# Revit family: Casement_30.5_D_Top_Hung_Standard
name_source: partatom
category: Windows
revit_build: Autodesk Revit 2014 (Build: 20130308_1515(x64)
units: mm (PartAtom-declared; Revit-internal decimal feet)

## types (12) — shared parameters
Aluminium Thickness = 1 mm  [stored 0.00328084 ft]
Bead SG Gap = 13 mm  [stored 0.0426509 ft]
Bottom Hung = No
Casement Dimension = 31 mm  [stored 0.101706 ft]
Custom Sash Height = 554 mm  [stored 1.81759 ft]
DG Extrusion Start = 5 mm  [stored 0.0164042 ft]
DG Gasket Finish = Double Glazing Gasket Material
DG Thickness = 3 mm  [stored 0.00984252 ft]
DG Thickness Calc = 3 mm  [stored 0.00984252 ft]
Default Sill Height = 800 mm  [stored 2.62467 ft]
Depth Bead = 17 mm
Description = Window 30.5mm, Type D top hung
Double Glazing = No
Frame Center Offset = 15 mm  [stored 0.0492126 ft]
Height Panel 1 = 540 mm  [stored 1.77165 ft]
Height Sash = 524 mm  [stored 1.71916 ft]
Height Sash Opening = 554 mm  [stored 1.81759 ft]
Limit Fixed Pane Height Max = 1800 mm  [stored 5.90551 ft]
Limit Fixed Pane Height Min = 200 mm  [stored 0.656168 ft]
Limit Sash Height Max = 750 mm  [stored 2.46063 ft]
Limit Sash Height Min = 300 mm  [stored 0.984252 ft]
Limit Sash Width Max = 1000 mm  [stored 3.28084 ft]
Limit Sash Width Min = 300 mm  [stored 0.984252 ft]
Limit Window Height Max = 2430 mm
Limit Window Height Min = 830 mm  [stored 2.7231 ft]
Limit Window Width Max = 1046 mm  [stored 3.43176 ft]
Limit Window Width Min = 346 mm
Manufacturer = Crealco
Max System DG One Piece Thickness = 3 mm  [stored 0.00984252 ft]
Max System DG Unit Thickness = 18 mm  [stored 0.0590551 ft]
Model = Casement 30.5
Offset Bead SG Center Reversed = 15 mm  [stored 0.0492126 ft]
Offset Panel 3 Bead Top = 600 mm  [stored 1.9685 ft]
Offset Sash Left = 23 mm  [stored 0.0754593 ft]
Offset Sash Top = 23 mm  [stored 0.0754593 ft]
Offset Transom Top = 570 mm  [stored 1.87008 ft]
Offset Window Exterior = 15 mm  [stored 0.0492126 ft]
SG Gasket Thickness = 6 mm  [stored 0.019685 ft]
Sash Center Offset = 12 mm  [stored 0.0393701 ft]
Sash Overlap = 7 mm  [stored 0.0229659 ft]
Sash Spacing Inner = 8 mm  [stored 0.0262467 ft]
Top Hung = Yes
URL = http://www.crealco.co.za
Wall Closure = By host
Width Bead = 15 mm  [stored 0.0492126 ft]
Width Profile = 30 mm  [stored 0.0984252 ft]
zero-valued in all types: Window Exterior Offset

## per-type parameters (varying)
| type | Area Pane Bottom | Area Pane Top | Clearvue SHGC Value | Clearvue U Value | Custom Windload | Custom Window Height | Custom Window Width | Energy Advantage SHGC Value | Energy Advantage U Value | Height | Height Panel 3 | Intruderprufe LowE SHGC Value | Intruderprufe LowE U Value | Intruderprufe SHGC Value | Intruderprufe U Value | Length Transom | Max Pane Area | Width | Width Panel 1 | Width Panel 3 | Width Sash | Width Sash Opening | Windload Design |
| 305-0609T-1000Pa | 0.13 m² | 0.23 m² | 0.518 | 6.18 | 1000 mm  [stored 3.28084 ft] | 890 mm  [stored 2.91995 ft] | 590 mm  [stored 1.9357 ft] | 0.465 | 4.98 | 890 mm  [stored 2.91995 ft] | 260 mm | 0.441 | 4.87 | 0.493 | 6.04 | 530 mm  [stored 1.73885 ft] | 0.23 m² | 590 mm  [stored 1.9357 ft] | 530 mm  [stored 1.73885 ft] | 530 mm  [stored 1.73885 ft] | 514 mm  [stored 1.68635 ft] | 544 mm  [stored 1.78478 ft] | 1000 mm  [stored 3.28084 ft] |
| 305-0909T-1000Pa | 0.21 m² | 0.37 m² | 0.564 | 6.14 | 1000 mm  [stored 3.28084 ft] | 890 mm  [stored 2.91995 ft] | 890 mm  [stored 2.91995 ft] | 0.506 | 4.81 | 890 mm  [stored 2.91995 ft] | 260 mm | 0.478 | 4.7 | 0.537 | 6 | 830 mm  [stored 2.7231 ft] | 0.37 m² | 890 mm  [stored 2.91995 ft] | 830 mm  [stored 2.7231 ft] | 830 mm  [stored 2.7231 ft] | 814 mm  [stored 2.6706 ft] | 844 mm  [stored 2.76903 ft] | 1000 mm  [stored 3.28084 ft] |
| 305-0612T-1000Pa | 0.29 m² | 0.23 m² | 0.566 | 6.12 | 1000 mm  [stored 3.28084 ft] | 1190 mm  [stored 3.9042 ft] | 590 mm  [stored 1.9357 ft] | 0.508 | 4.79 | 1190 mm  [stored 3.9042 ft] | 560 mm | 0.48 | 4.68 | 0.539 | 5.99 | 530 mm  [stored 1.73885 ft] | 0.29 m² | 590 mm  [stored 1.9357 ft] | 530 mm  [stored 1.73885 ft] | 530 mm  [stored 1.73885 ft] | 514 mm  [stored 1.68635 ft] | 544 mm  [stored 1.78478 ft] | 1000 mm  [stored 3.28084 ft] |
| 305-0912T-1000Pa | 0.45 m² | 0.37 m² | 0.613 | 6.09 | 1000 mm  [stored 3.28084 ft] | 1190 mm  [stored 3.9042 ft] | 890 mm  [stored 2.91995 ft] | 0.549 | 4.62 | 1190 mm  [stored 3.9042 ft] | 560 mm | 0.517 | 4.51 | 0.583 | 5.95 | 830 mm  [stored 2.7231 ft] | 0.45 m² | 890 mm  [stored 2.91995 ft] | 830 mm  [stored 2.7231 ft] | 830 mm  [stored 2.7231 ft] | 814 mm  [stored 2.6706 ft] | 844 mm  [stored 2.76903 ft] | 1000 mm  [stored 3.28084 ft] |
| 305-0609T-1500Pa | 0.13 m² | 0.23 m² | 0.518 | 6.18 | 1500 mm  [stored 4.92126 ft] | 890 mm  [stored 2.91995 ft] | 590 mm  [stored 1.9357 ft] | 0.465 | 4.98 | 890 mm  [stored 2.91995 ft] | 260 mm | 0.441 | 4.87 | 0.493 | 6.04 | 530 mm  [stored 1.73885 ft] | 0.23 m² | 590 mm  [stored 1.9357 ft] | 530 mm  [stored 1.73885 ft] | 530 mm  [stored 1.73885 ft] | 514 mm  [stored 1.68635 ft] | 544 mm  [stored 1.78478 ft] | 1500 mm  [stored 4.92126 ft] |
| 305-0609T-2000Pa | 0.13 m² | 0.23 m² | 0.518 | 6.18 | 2000 mm | 890 mm  [stored 2.91995 ft] | 590 mm  [stored 1.9357 ft] | 0.465 | 4.98 | 890 mm  [stored 2.91995 ft] | 260 mm | 0.441 | 4.87 | 0.493 | 6.04 | 530 mm  [stored 1.73885 ft] | 0.23 m² | 590 mm  [stored 1.9357 ft] | 530 mm  [stored 1.73885 ft] | 530 mm  [stored 1.73885 ft] | 514 mm  [stored 1.68635 ft] | 544 mm  [stored 1.78478 ft] | 2000 mm |
| 305-0612T-1500Pa | 0.29 m² | 0.23 m² | 0.566 | 6.12 | 1500 mm  [stored 4.92126 ft] | 1190 mm  [stored 3.9042 ft] | 590 mm  [stored 1.9357 ft] | 0.508 | 4.79 | 1190 mm  [stored 3.9042 ft] | 560 mm | 0.48 | 4.68 | 0.539 | 5.99 | 530 mm  [stored 1.73885 ft] | 0.29 m² | 590 mm  [stored 1.9357 ft] | 530 mm  [stored 1.73885 ft] | 530 mm  [stored 1.73885 ft] | 514 mm  [stored 1.68635 ft] | 544 mm  [stored 1.78478 ft] | 1500 mm  [stored 4.92126 ft] |
| 305-0612T-2000Pa | 0.29 m² | 0.23 m² | 0.566 | 6.12 | 2000 mm | 1190 mm  [stored 3.9042 ft] | 590 mm  [stored 1.9357 ft] | 0.508 | 4.79 | 1190 mm  [stored 3.9042 ft] | 560 mm | 0.48 | 4.68 | 0.539 | 5.99 | 530 mm  [stored 1.73885 ft] | 0.29 m² | 590 mm  [stored 1.9357 ft] | 530 mm  [stored 1.73885 ft] | 530 mm  [stored 1.73885 ft] | 514 mm  [stored 1.68635 ft] | 544 mm  [stored 1.78478 ft] | 2000 mm |
| 305-0909T-1500Pa | 0.21 m² | 0.37 m² | 0.564 | 6.14 | 1500 mm  [stored 4.92126 ft] | 890 mm  [stored 2.91995 ft] | 890 mm  [stored 2.91995 ft] | 0.506 | 4.81 | 890 mm  [stored 2.91995 ft] | 260 mm | 0.478 | 4.7 | 0.537 | 6 | 830 mm  [stored 2.7231 ft] | 0.37 m² | 890 mm  [stored 2.91995 ft] | 830 mm  [stored 2.7231 ft] | 830 mm  [stored 2.7231 ft] | 814 mm  [stored 2.6706 ft] | 844 mm  [stored 2.76903 ft] | 1500 mm  [stored 4.92126 ft] |
| 305-0909T-2000Pa | 0.21 m² | 0.37 m² | 0.564 | 6.14 | 2000 mm | 890 mm  [stored 2.91995 ft] | 890 mm  [stored 2.91995 ft] | 0.506 | 4.81 | 890 mm  [stored 2.91995 ft] | 260 mm | 0.478 | 4.7 | 0.537 | 6 | 830 mm  [stored 2.7231 ft] | 0.37 m² | 890 mm  [stored 2.91995 ft] | 830 mm  [stored 2.7231 ft] | 830 mm  [stored 2.7231 ft] | 814 mm  [stored 2.6706 ft] | 844 mm  [stored 2.76903 ft] | 2000 mm |
| 305-0912T-1500Pa | 0.45 m² | 0.37 m² | 0.613 | 6.09 | 1500 mm  [stored 4.92126 ft] | 1190 mm  [stored 3.9042 ft] | 890 mm  [stored 2.91995 ft] | 0.549 | 4.62 | 1190 mm  [stored 3.9042 ft] | 560 mm | 0.517 | 4.51 | 0.583 | 5.95 | 830 mm  [stored 2.7231 ft] | 0.45 m² | 890 mm  [stored 2.91995 ft] | 830 mm  [stored 2.7231 ft] | 830 mm  [stored 2.7231 ft] | 814 mm  [stored 2.6706 ft] | 844 mm  [stored 2.76903 ft] | 1500 mm  [stored 4.92126 ft] |
| 305-0912T-2000Pa | 0.45 m² | 0.37 m² | 0.613 | 6.09 | 2000 mm | 1190 mm  [stored 3.9042 ft] | 890 mm  [stored 2.91995 ft] | 0.549 | 4.62 | 1190 mm  [stored 3.9042 ft] | 560 mm | 0.517 | 4.51 | 0.583 | 5.95 | 830 mm  [stored 2.7231 ft] | 0.45 m² | 890 mm  [stored 2.91995 ft] | 830 mm  [stored 2.7231 ft] | 830 mm  [stored 2.7231 ft] | 814 mm  [stored 2.6706 ft] | 844 mm  [stored 2.76903 ft] | 2000 mm |

note: [stored X ft] marks values corroborated as IEEE doubles in the binary element streams (Revit-internal decimal feet)

## geometry (parser evidence)
native form markers: Blend x4, Extrusion x1, Sweep x27
no freeform markers — native parametric forms only
